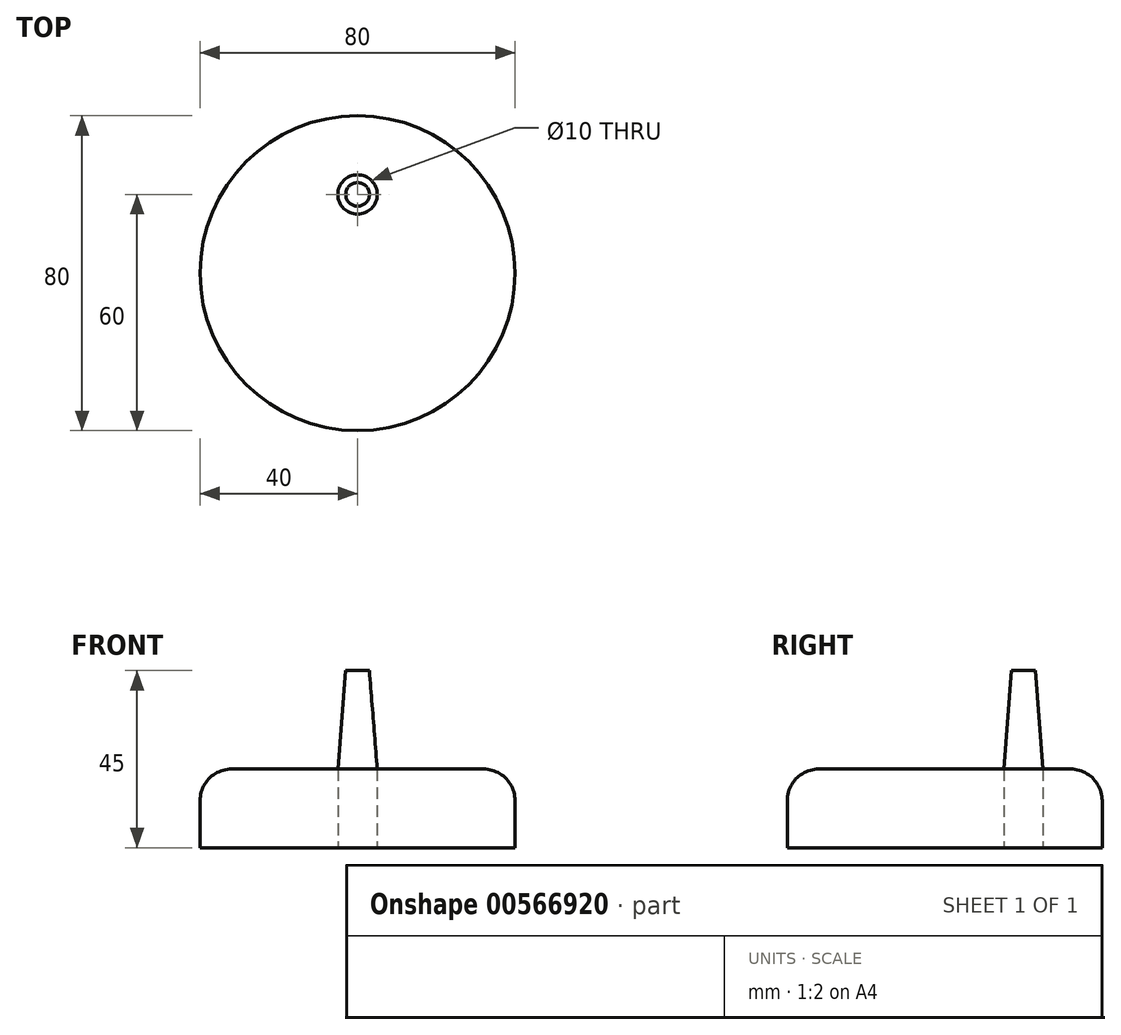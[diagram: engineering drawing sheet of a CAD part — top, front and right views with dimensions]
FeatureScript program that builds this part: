
annotation { "Feature Type Name" : "Feature", "Feature Type Description" : "" }
export const myFeature = defineFeature(function(context is Context, id is Id, definition is map)
    precondition{}
    {
        {
            var Q0;
            Q0=qCreatedBy(makeId("Top.planeOp"),FACE);
            var sketch = newSketch(context, id + "F0", { "sketchPlane" : qUnion([Q0])});
            skCircle(sketch, "E0", {"center": v(0, 0) * mm, "radius": 40 * mm});
            skCircle(sketch, "E1", {"center": v(0, 20) * mm, "radius": 5 * mm});
            skSolve(sketch);
        }
        {
            var Q0;
            Q0=makeQuery(id+"F0.imprint","IMPRINT",FACE,{"disambiguationData":[TD([[makeQuery(id+"F0.imprint","IMPRINT",EDGE,{"derivedFrom":sQuery(id+"F0.wireOp",EDGE,"E0")}),1.0]])]});
            extrude(context, id + "F1", {"entities" : qUnion([Q0]), "depth" : 20 * mm, "offsetDistance" : 25 * mm});
        }
        {
            var Q0;
            Q0=makeQuery(id+"F1.opExtrude","CAP_EDGE",EDGE,{"disambiguationData":[OSD([sQuery(id+"F0.wireOp",EDGE,"E0")])],"isStart":false});
            fillet(context, id + "F2", {"entities" : qUnion([Q0]), "radius" : 8 * mm, "tangentPropagation" : true, "allowEdgeOverflow" : false});
        }
        {
            var Q0;
            Q0=makeQuery(id+"F0.imprint","IMPRINT",FACE,{"disambiguationData":[TD([[makeQuery(id+"F0.imprint","IMPRINT",EDGE,{"derivedFrom":sQuery(id+"F0.wireOp",EDGE,"E1")}),1.0]])]});
            extrude(context, id + "F3", {"entities" : qUnion([Q0]), "depth" : 45 * mm, "offsetDistance" : 25 * mm});
        }
        {
            var Q0;
            Q0=makeQuery(id+"F3.opExtrude","CAP_FACE",FACE,{"disambiguationData":[OSD([sQuery(id+"F0.wireOp",EDGE,"E1")])],"isStart":false});
            chamfer(context, id + "F4", {"entities" : qUnion([Q0]), "chamferType" : ChamferType.TWO_OFFSETS, "width1" : 2 * mm, "oppositeDirection" : false, "width2" : 25 * mm});
        }
    });
